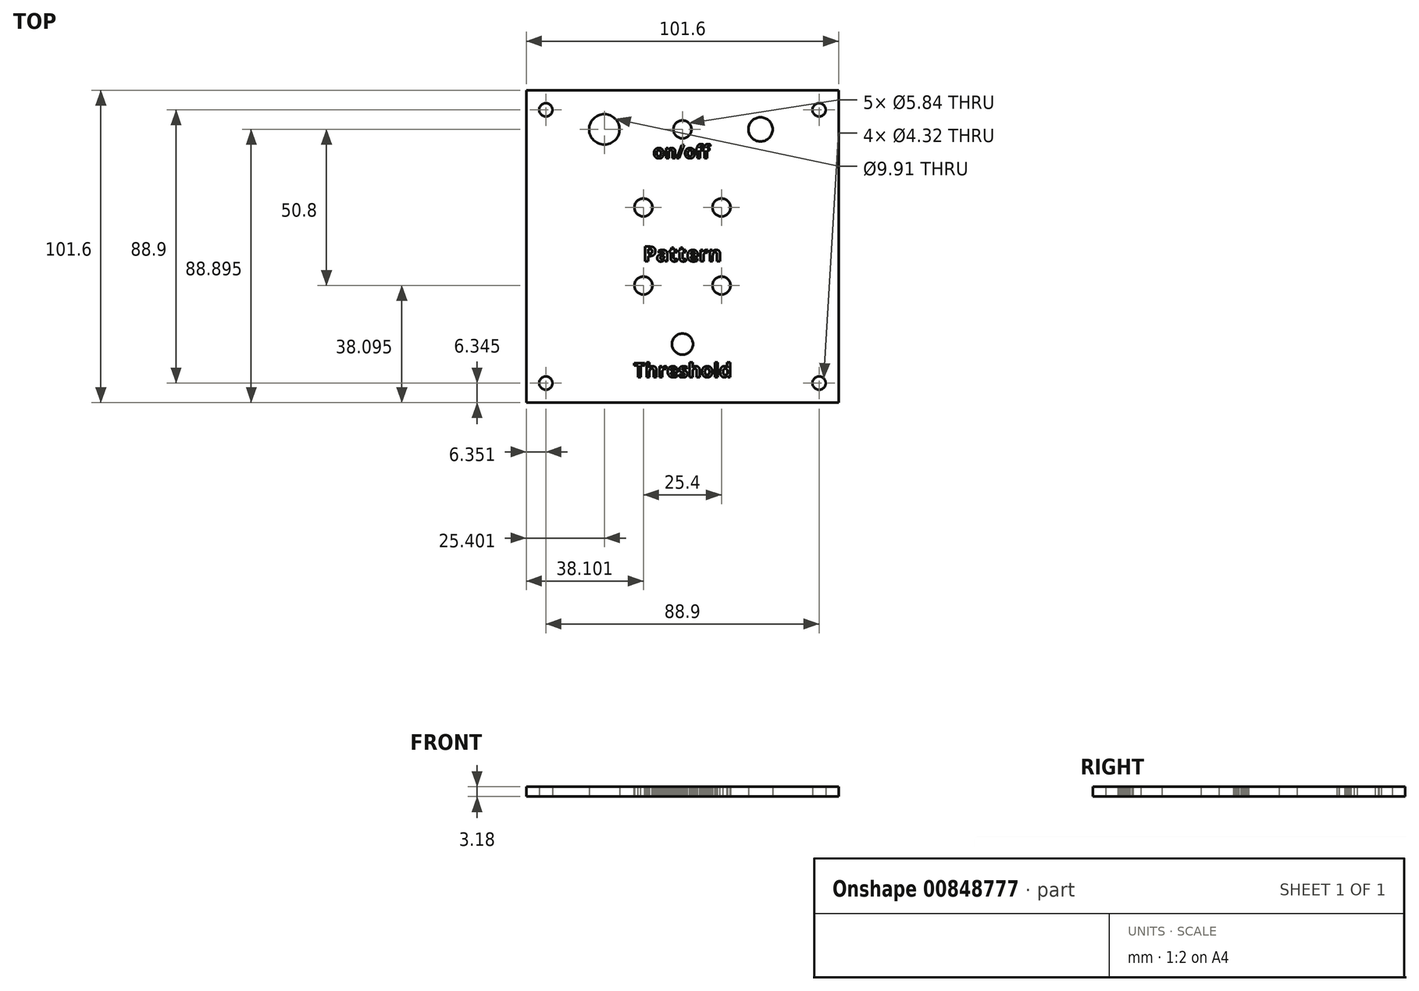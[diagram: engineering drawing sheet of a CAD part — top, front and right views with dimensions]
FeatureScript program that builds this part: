
annotation { "Feature Type Name" : "Feature", "Feature Type Description" : "" }
export const myFeature = defineFeature(function(context is Context, id is Id, definition is map)
    precondition{}
    {
        {
            var Q0;
            Q0=qCreatedBy(makeId("Top.planeOp"),FACE);
            var sketch = newSketch(context, id + "F0", { "sketchPlane" : qUnion([Q0])});
            skLineSegment(sketch, "E0.bottom", {"start": v(-85.78, 56.49) * mm, "end": v(15.82, 56.49) * mm});
            skLineSegment(sketch, "E0.top", {"start": v(-85.78, -45.11) * mm, "end": v(15.82, -45.11) * mm});
            skLineSegment(sketch, "E0.left", {"start": v(-85.78, 56.49) * mm, "end": v(-85.78, -45.11) * mm});
            skLineSegment(sketch, "E0.right", {"start": v(15.82, 56.49) * mm, "end": v(15.82, -45.11) * mm});
            skCircle(sketch, "E1", {"center": v(-79.43, 50.14) * mm, "radius": 2.16 * mm});
            skCircle(sketch, "E2.0.1.0", {"center": v(-79.43, -38.76) * mm, "radius": 2.16 * mm});
            skCircle(sketch, "E2.1.0.0", {"center": v(9.47, 50.14) * mm, "radius": 2.16 * mm});
            skCircle(sketch, "E2.1.1.0", {"center": v(9.47, -38.76) * mm, "radius": 2.16 * mm});
            skLineSegment(sketch, "E2.direction1", {"start": v(-79.43, 50.14) * mm, "end": v(9.47, 50.14) * mm, "construction": true});
            skLineSegment(sketch, "E2.direction2", {"start": v(-79.43, 50.14) * mm, "end": v(-79.43, -38.76) * mm, "construction": true});
            skCircle(sketch, "E3", {"center": v(-60.38, 43.79) * mm, "radius": 4.95 * mm});
            skCircle(sketch, "E4", {"center": v(-9.58, 43.79) * mm, "radius": 3.94 * mm});
            skCircle(sketch, "E5", {"center": v(-34.98, -26.06) * mm, "radius": 3.43 * mm});
            skCircle(sketch, "E6", {"center": v(-34.98, 43.79) * mm, "radius": 2.92 * mm});
            skCircle(sketch, "E7", {"center": v(-47.68, 18.39) * mm, "radius": 2.92 * mm});
            skCircle(sketch, "E8.0.1.0", {"center": v(-47.68, -7.01) * mm, "radius": 2.92 * mm});
            skCircle(sketch, "E8.1.0.0", {"center": v(-22.28, 18.39) * mm, "radius": 2.92 * mm});
            skCircle(sketch, "E8.1.1.0", {"center": v(-22.28, -7.01) * mm, "radius": 2.92 * mm});
            skLineSegment(sketch, "E8.direction1", {"start": v(-47.68, 18.39) * mm, "end": v(-22.28, 18.39) * mm, "construction": true});
            skLineSegment(sketch, "E8.direction2", {"start": v(-47.68, 18.39) * mm, "end": v(-47.68, -7.01) * mm, "construction": true});
            skSolve(sketch);
        }
        {
            var Q0;
            Q0=makeQuery(id+"F0.imprint","IMPRINT",FACE,{"disambiguationData":[TD([[makeQuery(id+"F0.imprint","IMPRINT",EDGE,{"derivedFrom":sQuery(id+"F0.wireOp",EDGE,"E0.bottom")}),-1.0]])]});
            extrude(context, id + "F1", {"entities" : qUnion([Q0]), "depth" : 3.17 * mm, "offsetDistance" : 25.4 * mm});
        }
        {
            var Q0;
            Q0=makeQuery(id+"F1.opExtrude","CAP_FACE",FACE,{"disambiguationData":[OSD([sQuery(id+"F0.wireOp",EDGE,"E0.bottom"),sQuery(id+"F0.wireOp",EDGE,"E0.top"),sQuery(id+"F0.wireOp",EDGE,"E0.left"),sQuery(id+"F0.wireOp",EDGE,"E0.right"),sQuery(id+"F0.wireOp",EDGE,"E1"),sQuery(id+"F0.wireOp",EDGE,"E2.0.1.0"),sQuery(id+"F0.wireOp",EDGE,"E2.1.0.0"),sQuery(id+"F0.wireOp",EDGE,"E2.1.1.0"),sQuery(id+"F0.wireOp",EDGE,"E3"),sQuery(id+"F0.wireOp",EDGE,"E4"),sQuery(id+"F0.wireOp",EDGE,"E5"),sQuery(id+"F0.wireOp",EDGE,"E6"),sQuery(id+"F0.wireOp",EDGE,"E7"),sQuery(id+"F0.wireOp",EDGE,"E8.0.1.0"),sQuery(id+"F0.wireOp",EDGE,"E8.1.0.0"),sQuery(id+"F0.wireOp",EDGE,"E8.1.1.0")])],"isStart":false});
            var sketch = newSketch(context, id + "F2", { "sketchPlane" : qUnion([Q0])});
            skText(sketch, "E9", { "text": "on/off", "fontName": "OpenSans-Bold.ttf"});
            skText(sketch, "E10", { "text": "Pattern", "fontName": "OpenSans-Bold.ttf"});
            skText(sketch, "E11", { "text": "Threshold", "fontName": "OpenSans-Bold.ttf"});
            const initialGuessF2  = {"E9": [-0.0445, 0.0344, 1, 0, 0.0043], "E10": [-0.04768, 0.00086, 1, 0, 0.00482], "E11": [-0.05085, -0.03682, 1, 0, 0.0046]};
            skSetInitialGuess(sketch, initialGuessF2);
            skSolve(sketch);
        }
        {
            var Q0;
            Q0 = qSketchRegion(id + "F2", true);
            extrude(context, id + "F3", {"entities" : qUnion([Q0]), "operationType" : NewBodyOperationType.REMOVE, "oppositeDirection" : true, "depth" : 25.4 * mm, "offsetDistance" : 25.4 * mm});
        }
    });
